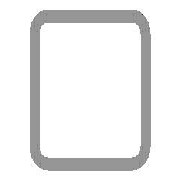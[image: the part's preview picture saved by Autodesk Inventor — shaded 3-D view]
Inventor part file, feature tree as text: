
AUTODESK INVENTOR PART (.ipt)
format: ipt  version: 2022 (Build 260153000, 153)  size: 145,920 bytes
history: native  units: mm (DEFAULTED — no unit token found)
features: other x4, sketch x3, plane x2, extrude x1, split x1
ambient origin geometry x8: Origin, YZ Plane, XZ Plane, XY Plane, X Axis, Y Axis, Z Axis, Center Point
bodies: Solid1 (feature_tree)
feature tree (11):
  parser-record x1  (decoder bookkeeping rows leaked as tree rows — omitted from the tree; the rows remain in map.json)
  other  "Driven Length"
  other  "Plano inicial"
  other  "Plano final"
  extrude  "Cuerpo"  TaperAngle=0.0deg  [1 undecoded]
  plane  "Plano de trabajo4"
  split  "Dividir1"
  sketch  "Boceto"  dims[d10=40.0mm d11=40.0mm d12=5.0mm d13=-0.0mm d14=420.0mm d15=20.0mm d16=20.0mm d17=90.0deg d18=420.0mm]
  sketch  "Sketch3"  dims[d3=420.0mm d4=0.0mm]
  plane  "Work Plane3"
  sketch  "Sketch4"  dims[d7=7.5mm]
note: 1 required parameter value undecoded (feature->parameter linkage not recoverable at this tier; creation-order binding heuristic only, values carry confidence <= 0.55)
